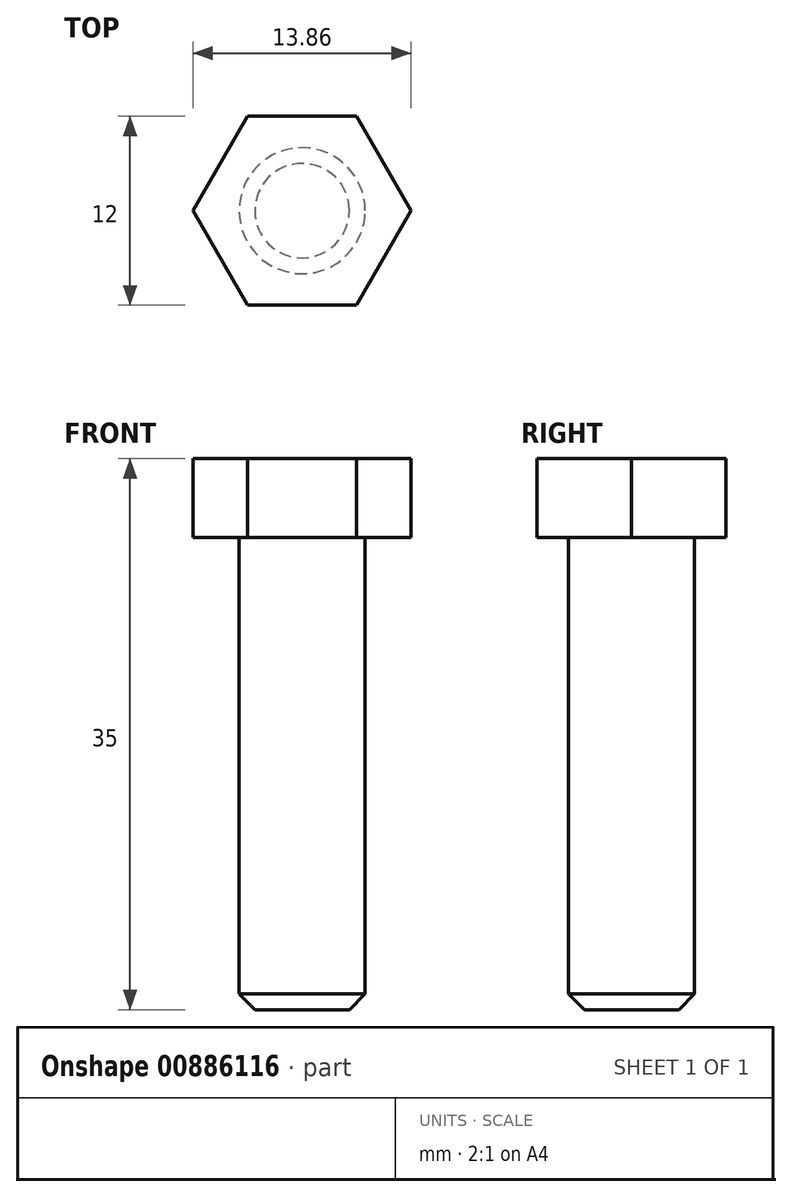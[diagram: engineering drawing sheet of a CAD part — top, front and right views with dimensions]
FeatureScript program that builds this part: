
annotation { "Feature Type Name" : "Feature", "Feature Type Description" : "" }
export const myFeature = defineFeature(function(context is Context, id is Id, definition is map)
    precondition{}
    {
        {
            var Q0;
            Q0=qCreatedBy(makeId("Top.planeOp"),FACE);
            var sketch = newSketch(context, id + "F0", { "sketchPlane" : qUnion([Q0])});
            skCircle(sketch, "E0.cCircle", {"center": v(0, 0) * mm, "radius": 6 * mm, "construction": true});
            skLineSegment(sketch, "E0.0", {"start": v(-3.46, 6) * mm, "end": v(3.46, 6) * mm});
            skLineSegment(sketch, "E0.1", {"start": v(3.46, 6) * mm, "end": v(6.93, 0) * mm});
            skLineSegment(sketch, "E0.2", {"start": v(6.93, 0) * mm, "end": v(3.46, -6) * mm});
            skLineSegment(sketch, "E0.3", {"start": v(3.46, -6) * mm, "end": v(-3.46, -6) * mm});
            skLineSegment(sketch, "E0.4", {"start": v(-3.46, -6) * mm, "end": v(-6.93, 0) * mm});
            skLineSegment(sketch, "E0.5", {"start": v(-6.93, 0) * mm, "end": v(-3.46, 6) * mm});
            skPoint(sketch, "E0.0.midPoint", {"position": v(0, 6) * mm});
            skSolve(sketch);
        }
        {
            var Q0;
            Q0 = qSketchRegion(id + "F0", true);
            extrude(context, id + "F1", {"entities" : qUnion([Q0]), "depth" : 5 * mm, "offsetDistance" : 25 * mm});
        }
        {
            var Q0;
            Q0=makeQuery(id+"F1.opExtrude","CAP_FACE",FACE,{"disambiguationData":[OSD([sQuery(id+"F0.wireOp",EDGE,"E0.0"),sQuery(id+"F0.wireOp",EDGE,"E0.1"),sQuery(id+"F0.wireOp",EDGE,"E0.2"),sQuery(id+"F0.wireOp",EDGE,"E0.3"),sQuery(id+"F0.wireOp",EDGE,"E0.4"),sQuery(id+"F0.wireOp",EDGE,"E0.5")])],"isStart":true});
            var sketch = newSketch(context, id + "F2", { "sketchPlane" : qUnion([Q0])});
            skCircle(sketch, "E1", {"center": v(0, 0) * mm, "radius": 4 * mm});
            skSolve(sketch);
        }
        {
            var Q0;
            Q0 = qSketchRegion(id + "F2", true);
            extrude(context, id + "F3", {"entities" : qUnion([Q0]), "operationType" : NewBodyOperationType.ADD, "depth" : 30 * mm, "offsetDistance" : 25 * mm});
        }
        {
            var Q0;
            Q0=makeQuery(id+"F3.opExtrude","CAP_EDGE",EDGE,{"disambiguationData":[OSD([sQuery(id+"F2.wireOp",EDGE,"E1")])],"isStart":false});
            chamfer(context, id + "F4", {"entities" : qUnion([Q0]), "width" : 1 * mm, "tangentPropagation" : true});
        }
    });
